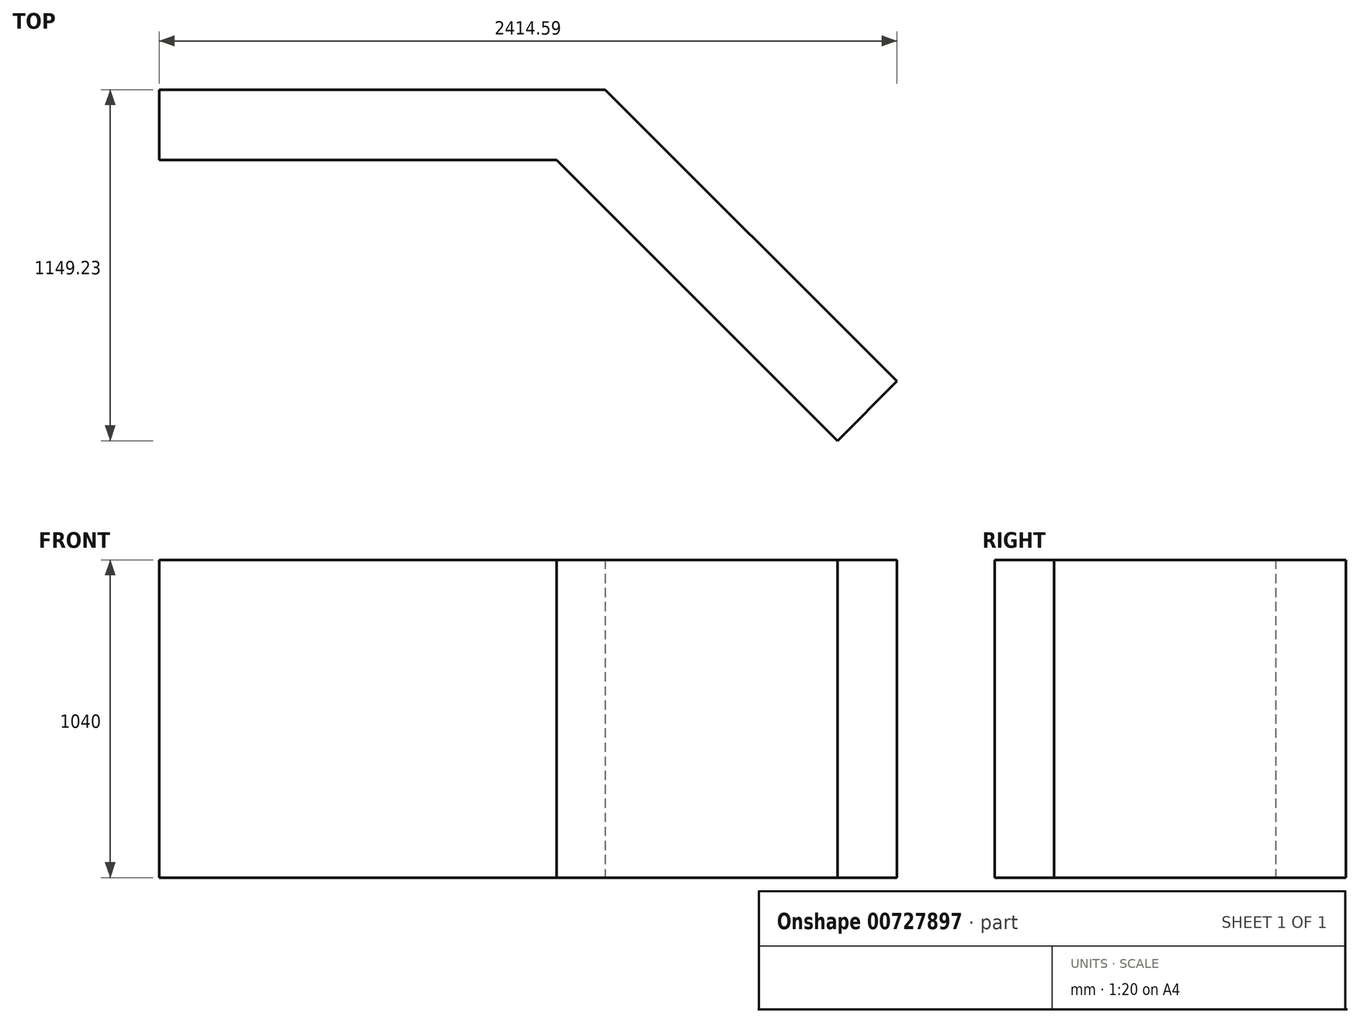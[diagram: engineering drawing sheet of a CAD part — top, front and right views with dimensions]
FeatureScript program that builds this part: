
annotation { "Feature Type Name" : "Feature", "Feature Type Description" : "" }
export const myFeature = defineFeature(function(context is Context, id is Id, definition is map)
    precondition{}
    {
        {
            var Q0;
            Q0=qCreatedBy(makeId("Top.planeOp"),FACE);
            var sketch = newSketch(context, id + "F0", { "sketchPlane" : qUnion([Q0])});
            skLineSegment(sketch, "E0", {"start": v(-988.92, 389.6) * mm, "end": v(471.08, 389.6) * mm});
            skLineSegment(sketch, "E1", {"start": v(471.08, 389.6) * mm, "end": v(1425.67, -565) * mm});
            skLineSegment(sketch, "E2", {"start": v(1425.67, -565) * mm, "end": v(1231.03, -759.64) * mm});
            skLineSegment(sketch, "E3", {"start": v(1231.03, -759.64) * mm, "end": v(311.79, 159.6) * mm});
            skLineSegment(sketch, "E4", {"start": v(311.79, 159.6) * mm, "end": v(-988.21, 159.6) * mm});
            skLineSegment(sketch, "E5", {"start": v(-988.21, 159.6) * mm, "end": v(-988.92, 389.6) * mm});
            skSolve(sketch);
        }
        {
            var Q0;
            Q0 = qSketchRegion(id + "F0", true);
            extrude(context, id + "F1", {"entities" : qUnion([Q0]), "endBound" : BoundingType.SYMMETRIC, "depth" : 1040 * mm, "offsetDistance" : 25 * mm});
        }
    });
